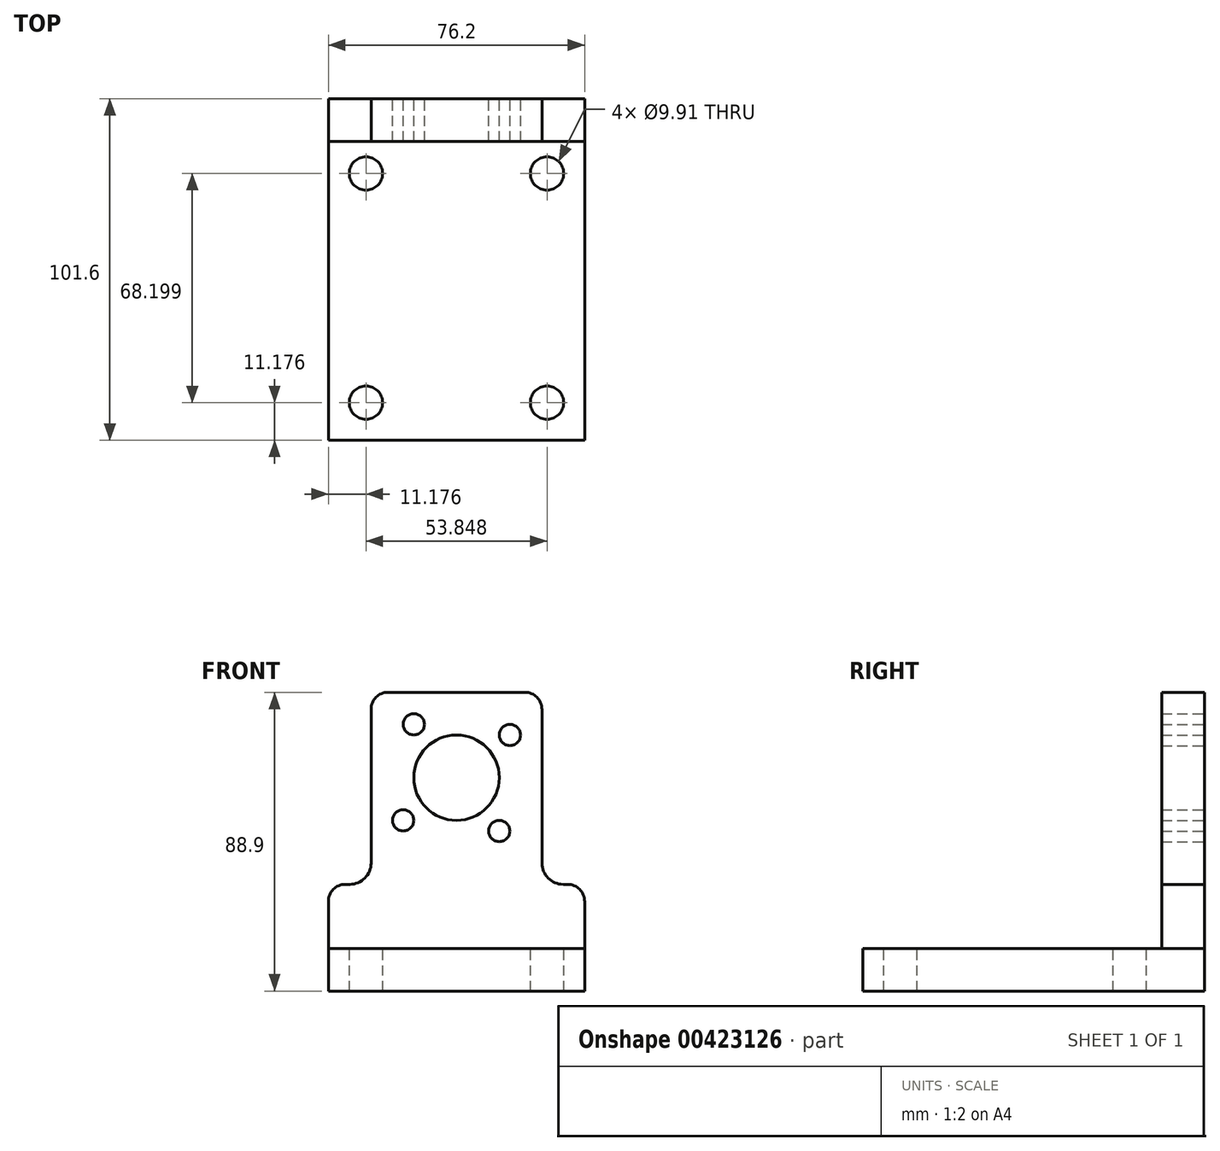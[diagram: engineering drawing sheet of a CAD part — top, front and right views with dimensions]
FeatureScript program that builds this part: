
annotation { "Feature Type Name" : "Feature", "Feature Type Description" : "" }
export const myFeature = defineFeature(function(context is Context, id is Id, definition is map)
    precondition{}
    {
        {
            var Q0;
            Q0=qCreatedBy(makeId("Top.planeOp"),FACE);
            var sketch = newSketch(context, id + "F0", { "sketchPlane" : qUnion([Q0])});
            skLineSegment(sketch, "E0.bottom", {"start": v(0, 0) * mm, "end": v(76.2, 0) * mm});
            skLineSegment(sketch, "E0.top", {"start": v(0, -101.6) * mm, "end": v(76.2, -101.6) * mm});
            skLineSegment(sketch, "E0.left", {"start": v(0, 0) * mm, "end": v(0, -101.6) * mm});
            skLineSegment(sketch, "E0.right", {"start": v(76.2, 0) * mm, "end": v(76.2, -101.6) * mm});
            skCircle(sketch, "E1", {"center": v(11.18, -22.23) * mm, "radius": 4.95 * mm});
            skCircle(sketch, "E2", {"center": v(11.18, -90.42) * mm, "radius": 4.95 * mm});
            skCircle(sketch, "E3", {"center": v(65.02, -90.42) * mm, "radius": 4.95 * mm});
            skCircle(sketch, "E4", {"center": v(65.02, -22.22) * mm, "radius": 4.95 * mm});
            skSolve(sketch);
        }
        {
            var Q0;
            Q0 = qSketchRegion(id + "F0", true);
            extrude(context, id + "F1", {"entities" : qUnion([Q0]), "oppositeDirection" : true, "depth" : 12.7 * mm});
        }
        {
            var Q0;
            Q0=qCreatedBy(makeId("Front.planeOp"),FACE);
            var sketch = newSketch(context, id + "F2", { "sketchPlane" : qUnion([Q0])});
            skLineSegment(sketch, "E5", {"start": v(0, 0) * mm, "end": v(0, 13.97) * mm});
            skLineSegment(sketch, "E6", {"start": v(76.2, 0) * mm, "end": v(76.2, 13.97) * mm});
            skLineSegment(sketch, "E7", {"start": v(0, 0) * mm, "end": v(76.2, 0) * mm});
            skCircle(sketch, "E8", {"center": v(38.1, 50.8) * mm, "radius": 12.7 * mm});
            skCircle(sketch, "E9", {"center": v(22.23, 38.1) * mm, "radius": 3.18 * mm});
            skCircle(sketch, "E10", {"center": v(25.4, 66.68) * mm, "radius": 3.18 * mm});
            skCircle(sketch, "E11", {"center": v(53.98, 63.5) * mm, "radius": 3.18 * mm});
            skCircle(sketch, "E12", {"center": v(50.8, 34.93) * mm, "radius": 3.18 * mm});
            skLineSegment(sketch, "E13", {"start": v(71.12, 19.05) * mm, "end": v(69.85, 19.05) * mm});
            skLineSegment(sketch, "E14", {"start": v(12.7, 25.4) * mm, "end": v(12.7, 71.12) * mm});
            skLineSegment(sketch, "E15", {"start": v(17.78, 76.2) * mm, "end": v(58.42, 76.2) * mm});
            skLineSegment(sketch, "E16", {"start": v(63.5, 71.12) * mm, "end": v(63.5, 25.4) * mm});
            skLineSegment(sketch, "E17.trimOffspring", {"start": v(6.35, 19.05) * mm, "end": v(5.08, 19.05) * mm});
            skPoint(sketch, "E18.visualSharp", {"position": v(12.7, 19.05) * mm});
            skArc(sketch, "E18.filletArc", {"start": v(6.35, 19.05) * mm, "mid": v(10.84, 20.9) * mm, "end": v(12.7, 25.4) * mm});
            skPoint(sketch, "E19.visualSharp", {"position": v(63.5, 19.05) * mm});
            skArc(sketch, "E19.filletArc", {"start": v(63.5, 25.4) * mm, "mid": v(65.36, 20.9) * mm, "end": v(69.85, 19.05) * mm});
            skPoint(sketch, "E20.visualSharp", {"position": v(12.7, 76.2) * mm});
            skArc(sketch, "E20.filletArc", {"start": v(17.78, 76.2) * mm, "mid": v(14.19, 74.71) * mm, "end": v(12.7, 71.12) * mm});
            skPoint(sketch, "E21.visualSharp", {"position": v(63.5, 76.2) * mm});
            skArc(sketch, "E21.filletArc", {"start": v(63.5, 71.12) * mm, "mid": v(62.01, 74.71) * mm, "end": v(58.42, 76.2) * mm});
            skPoint(sketch, "E22.visualSharp", {"position": v(76.2, 19.05) * mm});
            skArc(sketch, "E22.filletArc", {"start": v(76.2, 13.97) * mm, "mid": v(74.71, 17.56) * mm, "end": v(71.12, 19.05) * mm});
            skPoint(sketch, "E23.visualSharp", {"position": v(0, 19.05) * mm});
            skArc(sketch, "E23.filletArc", {"start": v(5.08, 19.05) * mm, "mid": v(1.49, 17.56) * mm, "end": v(0, 13.97) * mm});
            skSolve(sketch);
        }
        {
            var Q0;
            Q0 = qSketchRegion(id + "F2", true);
            extrude(context, id + "F3", {"entities" : qUnion([Q0]), "depth" : 12.7 * mm});
        }
    });
